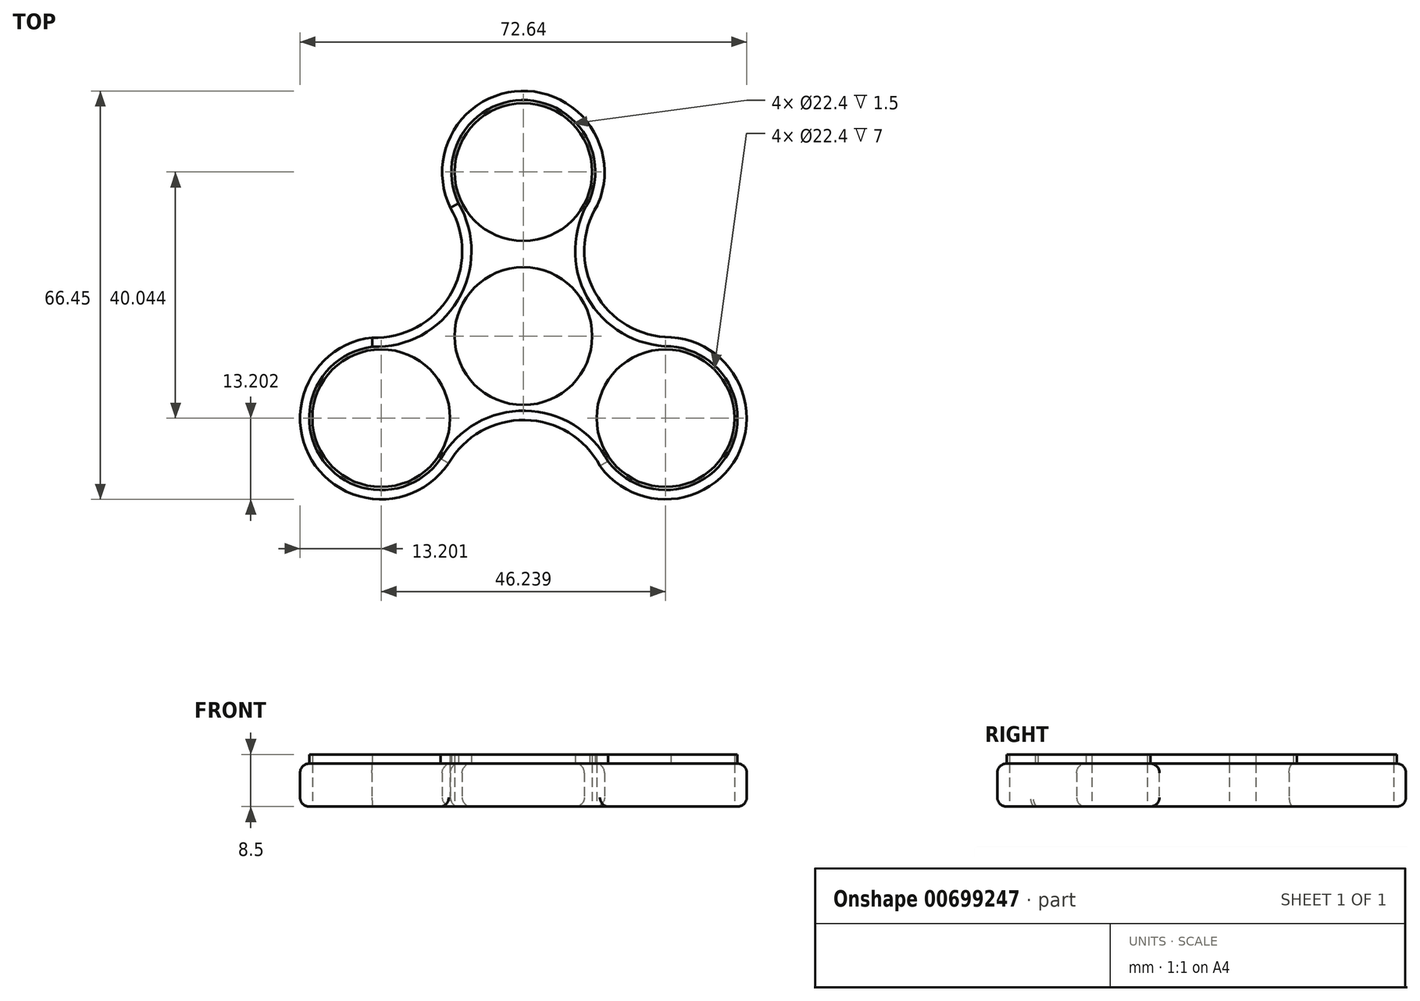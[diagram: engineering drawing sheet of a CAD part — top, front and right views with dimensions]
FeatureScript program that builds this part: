
annotation { "Feature Type Name" : "Feature", "Feature Type Description" : "" }
export const myFeature = defineFeature(function(context is Context, id is Id, definition is map)
    precondition{}
    {
        {
            var Q0;
            Q0=qCreatedBy(makeId("Top.planeOp"),FACE);
            var sketch = newSketch(context, id + "F0", { "sketchPlane" : qUnion([Q0])});
            skCircle(sketch, "E0", {"center": v(0, 0) * mm, "radius": 11.2 * mm});
            skCircle(sketch, "E1", {"center": v(0, 26.7) * mm, "radius": 11.2 * mm});
            skArc(sketch, "E2", {"start": v(11.11, 19.57) * mm, "mid": v(0.27, 39.9) * mm, "end": v(-11.4, 20.03) * mm});
            skArc(sketch, "E3.1.0", {"start": v(-22.5, -0.16) * mm, "mid": v(-34.68, -19.71) * mm, "end": v(-11.65, -19.89) * mm});
            skCircle(sketch, "E3.1.1", {"center": v(-23.12, -13.35) * mm, "radius": 11.2 * mm});
            skArc(sketch, "E3.2.0", {"start": v(11.4, -19.4) * mm, "mid": v(34.41, -20.18) * mm, "end": v(23.05, -0.15) * mm});
            skCircle(sketch, "E3.2.1", {"center": v(23.12, -13.35) * mm, "radius": 11.2 * mm});
            skArc(sketch, "E4", {"start": v(12.1, 21.43) * mm, "mid": v(11.67, 7.1) * mm, "end": v(24.03, -0.18) * mm});
            skArc(sketch, "E5.1.0", {"start": v(-24.61, -0.23) * mm, "mid": v(-11.98, 6.56) * mm, "end": v(-11.86, 20.9) * mm});
            skArc(sketch, "E5.2.0", {"start": v(12.5, -21.2) * mm, "mid": v(0.3, -13.65) * mm, "end": v(-12.17, -20.72) * mm});
            skSolve(sketch);
        }
        {
            var Q0;
            Q0=makeQuery(id+"F0.imprint","IMPRINT",FACE,{"disambiguationData":[TD([[makeQuery(id+"F0.imprint","IMPRINT",EDGE,{"derivedFrom":sQuery(id+"F0.wireOp",EDGE,"E0")}),-1.0]])]});
            extrude(context, id + "F1", {"entities" : qUnion([Q0]), "depth" : 7 * mm, "offsetDistance" : 25 * mm});
        }
        {
            var Q0;
            Q0=makeQuery(id+"F1.opExtrude","CAP_EDGE",EDGE,{"disambiguationData":[OSD([sQuery(id+"F0.wireOp",EDGE,"E5.2.0")])],"isStart":true});
            fillet(context, id + "F2", {"entities" : qUnion([Q0]), "radius" : 1.5 * mm, "tangentPropagation" : true, "allowEdgeOverflow" : false});
        }
        {
            var Q0;
            Q0=makeQuery(id+"F1.opExtrude","SWEPT_FACE",FACE,{"disambiguationData":[OSD([sQuery(id+"F0.wireOp",EDGE,"E4")])]});
            var Q1;
            Q1=makeQuery(id+"F1.opExtrude","CAP_EDGE",EDGE,{"disambiguationData":[OSD([sQuery(id+"F0.wireOp",EDGE,"E4")])],"isStart":true});
            var Q2;
            Q2=makeQuery(id+"F1.opExtrude","CAP_EDGE",EDGE,{"disambiguationData":[OSD([sQuery(id+"F0.wireOp",EDGE,"E3.2.0")])],"isStart":false});
            var Q3;
            Q3=makeQuery(id+"F1.opExtrude","CAP_EDGE",EDGE,{"disambiguationData":[OSD([sQuery(id+"F0.wireOp",EDGE,"E5.2.0")])],"isStart":false});
            var Q4;
            Q4=makeQuery(id+"F1.opExtrude","CAP_EDGE",EDGE,{"disambiguationData":[OSD([sQuery(id+"F0.wireOp",EDGE,"E3.1.0")])],"isStart":false});
            var Q5;
            Q5=makeQuery(id+"F1.opExtrude","CAP_EDGE",EDGE,{"disambiguationData":[OSD([sQuery(id+"F0.wireOp",EDGE,"E5.1.0")])],"isStart":false});
            var Q6;
            Q6=makeQuery(id+"F1.opExtrude","CAP_EDGE",EDGE,{"disambiguationData":[OSD([sQuery(id+"F0.wireOp",EDGE,"E2")])],"isStart":false});
            fillet(context, id + "F3", {"entities" : qUnion([Q0, Q1, Q2, Q3, Q4, Q5, Q6]), "radius" : 1.5 * mm, "tangentPropagation" : true, "allowEdgeOverflow" : false});
        }
        {
            var Q0;
            Q0=makeQuery(id+"F1.opExtrude","CAP_FACE",FACE,{"disambiguationData":[OSD([sQuery(id+"F0.wireOp",EDGE,"E0"),sQuery(id+"F0.wireOp",EDGE,"E1"),sQuery(id+"F0.wireOp",EDGE,"E2"),sQuery(id+"F0.wireOp",EDGE,"E3.1.0"),sQuery(id+"F0.wireOp",EDGE,"E3.1.1"),sQuery(id+"F0.wireOp",EDGE,"E3.2.0"),sQuery(id+"F0.wireOp",EDGE,"E3.2.1"),sQuery(id+"F0.wireOp",EDGE,"E4"),sQuery(id+"F0.wireOp",EDGE,"E5.1.0"),sQuery(id+"F0.wireOp",EDGE,"E5.2.0")])],"isStart":false});
            extrude(context, id + "F4", {"entities" : qUnion([Q0]), "depth" : 1.5 * mm, "offsetDistance" : 25 * mm});
        }
        {
            var Q0;
            Q0=makeQuery(id+"F1.opExtrude","CAP_EDGE",EDGE,{"disambiguationData":[OSD([sQuery(id+"F0.wireOp",EDGE,"E2")])],"isStart":true});
            var Q1;
            Q1=makeQuery(id+"F1.opExtrude","CAP_EDGE",EDGE,{"disambiguationData":[OSD([sQuery(id+"F0.wireOp",EDGE,"E5.1.0")])],"isStart":true});
            var Q2;
            Q2=makeQuery(id+"F1.opExtrude","CAP_EDGE",EDGE,{"disambiguationData":[OSD([sQuery(id+"F0.wireOp",EDGE,"E3.1.0")])],"isStart":true});
            var Q3;
            {var subQ0=sQuery(id+"F0.wireOp",EDGE,"E5.2.0");Q3=makeQuery(id+"F2.opFillet","BLEND_EDGE",EDGE,{"blendedFrom":[makeQuery(id+"F1.opExtrude","CAP_EDGE",EDGE,{"disambiguationData":[OSD([subQ0])],"isStart":true}),makeQuery(id+"F1.opExtrude","CAP_FACE",FACE,{"disambiguationData":[OSD([sQuery(id+"F0.wireOp",EDGE,"E0"),sQuery(id+"F0.wireOp",EDGE,"E1"),sQuery(id+"F0.wireOp",EDGE,"E2"),sQuery(id+"F0.wireOp",EDGE,"E3.1.0"),sQuery(id+"F0.wireOp",EDGE,"E3.1.1"),sQuery(id+"F0.wireOp",EDGE,"E3.2.0"),sQuery(id+"F0.wireOp",EDGE,"E3.2.1"),sQuery(id+"F0.wireOp",EDGE,"E4"),sQuery(id+"F0.wireOp",EDGE,"E5.1.0"),subQ0])],"isStart":true})],"blendedInto":[makeQuery(id+"F1.opExtrude","CAP_FACE",FACE,{"disambiguationData":[OSD([sQuery(id+"F0.wireOp",EDGE,"E0"),sQuery(id+"F0.wireOp",EDGE,"E1"),sQuery(id+"F0.wireOp",EDGE,"E2"),sQuery(id+"F0.wireOp",EDGE,"E3.1.0"),sQuery(id+"F0.wireOp",EDGE,"E3.1.1"),sQuery(id+"F0.wireOp",EDGE,"E3.2.0"),sQuery(id+"F0.wireOp",EDGE,"E3.2.1"),sQuery(id+"F0.wireOp",EDGE,"E4"),sQuery(id+"F0.wireOp",EDGE,"E5.1.0"),subQ0])],"isStart":true})]});}
            var Q4;
            Q4=makeQuery(id+"F1.opExtrude","CAP_EDGE",EDGE,{"disambiguationData":[OSD([sQuery(id+"F0.wireOp",EDGE,"E3.2.0")])],"isStart":true});
            var Q5;
            {var subQ0=sQuery(id+"F0.wireOp",EDGE,"E4");Q5=makeQuery(id+"F3.opFillet","BLEND_EDGE",EDGE,{"blendedFrom":[makeQuery(id+"F1.opExtrude","CAP_EDGE",EDGE,{"disambiguationData":[OSD([subQ0])],"isStart":true}),makeQuery(id+"F1.opExtrude","CAP_FACE",FACE,{"disambiguationData":[OSD([sQuery(id+"F0.wireOp",EDGE,"E0"),sQuery(id+"F0.wireOp",EDGE,"E1"),sQuery(id+"F0.wireOp",EDGE,"E2"),sQuery(id+"F0.wireOp",EDGE,"E3.1.0"),sQuery(id+"F0.wireOp",EDGE,"E3.1.1"),sQuery(id+"F0.wireOp",EDGE,"E3.2.0"),sQuery(id+"F0.wireOp",EDGE,"E3.2.1"),subQ0,sQuery(id+"F0.wireOp",EDGE,"E5.1.0"),sQuery(id+"F0.wireOp",EDGE,"E5.2.0")])],"isStart":true})],"blendedInto":[makeQuery(id+"F1.opExtrude","CAP_FACE",FACE,{"disambiguationData":[OSD([sQuery(id+"F0.wireOp",EDGE,"E0"),sQuery(id+"F0.wireOp",EDGE,"E1"),sQuery(id+"F0.wireOp",EDGE,"E2"),sQuery(id+"F0.wireOp",EDGE,"E3.1.0"),sQuery(id+"F0.wireOp",EDGE,"E3.1.1"),sQuery(id+"F0.wireOp",EDGE,"E3.2.0"),sQuery(id+"F0.wireOp",EDGE,"E3.2.1"),subQ0,sQuery(id+"F0.wireOp",EDGE,"E5.1.0"),sQuery(id+"F0.wireOp",EDGE,"E5.2.0")])],"isStart":true})]});}
            fillet(context, id + "F5", {"entities" : qUnion([Q0, Q1, Q2, Q3, Q4, Q5]), "radius" : 1.5 * mm, "tangentPropagation" : true, "allowEdgeOverflow" : false});
        }
    });
